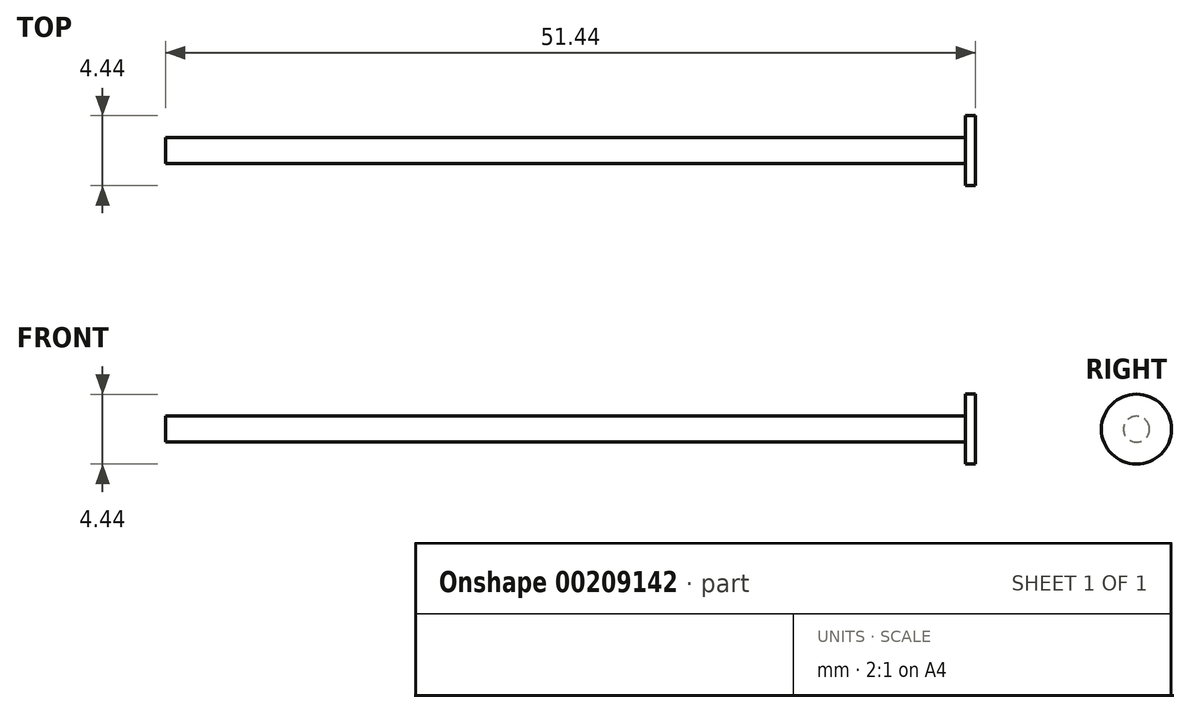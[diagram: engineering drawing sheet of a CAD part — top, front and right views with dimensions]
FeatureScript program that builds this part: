
annotation { "Feature Type Name" : "Feature", "Feature Type Description" : "" }
export const myFeature = defineFeature(function(context is Context, id is Id, definition is map)
    precondition{}
    {
        {
            var Q0;
            Q0=qCreatedBy(makeId("Right.planeOp"),FACE);
            var sketch = newSketch(context, id + "F0", { "sketchPlane" : qUnion([Q0])});
            skCircle(sketch, "E0", {"center": v(0, 0) * mm, "radius": 2.22 * mm});
            skSolve(sketch);
        }
        {
            var Q0;
            Q0=makeQuery(id+"F0.imprint","IMPRINT",FACE,{"disambiguationData":[TD([[makeQuery(id+"F0.imprint","IMPRINT",EDGE,{"derivedFrom":sQuery(id+"F0.wireOp",EDGE,"E0")}),1.0]])]});
            extrude(context, id + "F1", {"entities" : qUnion([Q0]), "depth" : 0.64 * mm});
        }
        {
            var Q0;
            Q0=makeQuery(id+"F1.opExtrude","CAP_FACE",FACE,{"disambiguationData":[OSD([sQuery(id+"F0.wireOp",EDGE,"E0")])],"isStart":true});
            var sketch = newSketch(context, id + "F2", { "sketchPlane" : qUnion([Q0])});
            skCircle(sketch, "E1", {"center": v(0, 0) * mm, "radius": 0.83 * mm});
            skSolve(sketch);
        }
        {
            var Q0;
            Q0=makeQuery(id+"F2.imprint","IMPRINT",FACE,{"disambiguationData":[TD([[makeQuery(id+"F2.imprint","IMPRINT",EDGE,{"derivedFrom":sQuery(id+"F2.wireOp",EDGE,"E1")}),1.0]])]});
            var Q1;
            Q1=sQuery(id+"F2.wireOp",EDGE,"E1");
            extrude(context, id + "F3", {"entities" : qUnion([Q0]), "operationType" : NewBodyOperationType.ADD, "surfaceEntities" : qUnion([Q1]), "depth" : 50.8 * mm});
        }
    });
